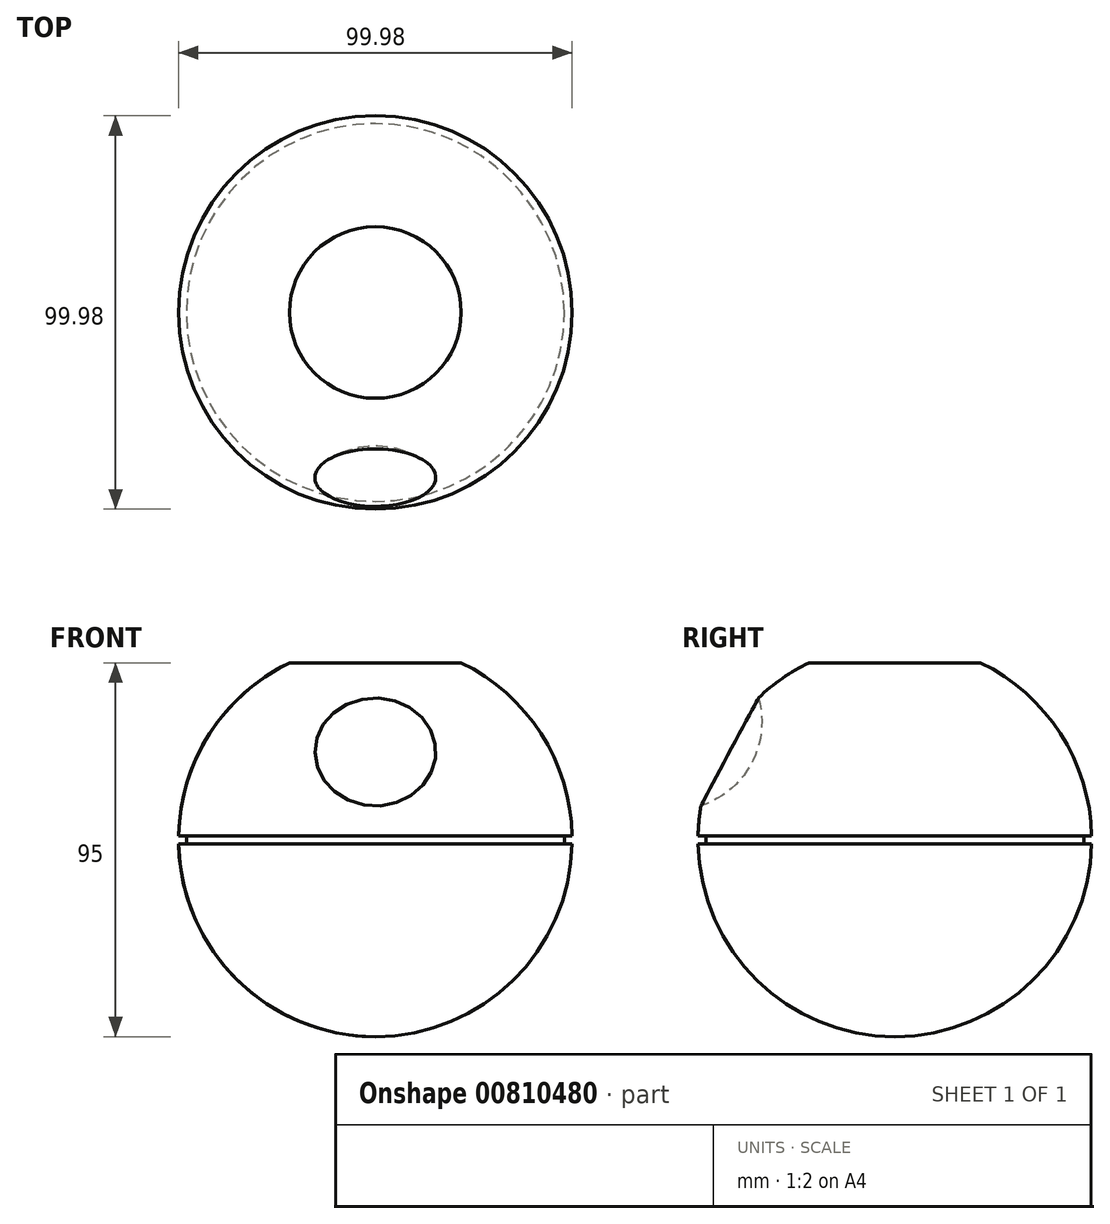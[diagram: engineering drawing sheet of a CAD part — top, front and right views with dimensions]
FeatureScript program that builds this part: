
annotation { "Feature Type Name" : "Feature", "Feature Type Description" : "" }
export const myFeature = defineFeature(function(context is Context, id is Id, definition is map)
    precondition{}
    {
        {
            var Q0;
            Q0=qCreatedBy(makeId("Front.planeOp"),FACE);
            var sketch = newSketch(context, id + "F0", { "sketchPlane" : qUnion([Q0])});
            skArc(sketch, "E0", {"start": v(0, -50) * mm, "mid": v(50, 0) * mm, "end": v(0, 50) * mm});
            skLineSegment(sketch, "E1", {"start": v(0, 50) * mm, "end": v(0, -50) * mm});
            skSolve(sketch);
        }
        {
            var Q0;
            Q0=makeQuery(id+"F0.imprint","IMPRINT",FACE,{"disambiguationData":[TD([[makeQuery(id+"F0.imprint","IMPRINT",EDGE,{"derivedFrom":sQuery(id+"F0.wireOp",EDGE,"E0")}),1.0]])]});
            var Q1;
            Q1=sQuery(id+"F0.wireOp",EDGE,"E1");
            revolve(context, id + "F1", {"entities" : qUnion([Q0]), "axis" : qUnion([Q1]), "revolveType" : RevolveType.FULL});
        }
        {
            var Q0;
            Q0=qCreatedBy(makeId("Right.planeOp"),FACE);
            var sketch = newSketch(context, id + "F2", { "sketchPlane" : qUnion([Q0])});
            skArc(sketch, "E2", {"start": v(-56.53, 7.5) * mm, "mid": v(-33.82, 29.24) * mm, "end": v(-55, 52.46) * mm});
            skLineSegment(sketch, "E3", {"start": v(-55, 52.46) * mm, "end": v(-56.53, 7.5) * mm});
            skSolve(sketch);
        }
        {
            var Q0;
            Q0=makeQuery(id+"F2.imprint","IMPRINT",FACE,{"disambiguationData":[TD([[makeQuery(id+"F2.imprint","IMPRINT",EDGE,{"derivedFrom":sQuery(id+"F2.wireOp",EDGE,"E2")}),1.0]])]});
            var Q1;
            Q1=sQuery(id+"F2.wireOp",EDGE,"E3");
            revolve(context, id + "F3", {"operationType" : NewBodyOperationType.REMOVE, "entities" : qUnion([Q0]), "axis" : qUnion([Q1]), "revolveType" : RevolveType.FULL, "oppositeDirection" : true});
        }
        {
            var Q0;
            Q0=qCreatedBy(makeId("Front.planeOp"),FACE);
            var sketch = newSketch(context, id + "F4", { "sketchPlane" : qUnion([Q0])});
            skLineSegment(sketch, "E4.bottom", {"start": v(-63.8, 61.9) * mm, "end": v(62.76, 61.9) * mm});
            skLineSegment(sketch, "E4.top", {"start": v(-63.8, 45) * mm, "end": v(62.76, 45) * mm});
            skLineSegment(sketch, "E4.left", {"start": v(-63.8, 61.9) * mm, "end": v(-63.8, 45) * mm});
            skLineSegment(sketch, "E4.right", {"start": v(62.76, 61.9) * mm, "end": v(62.76, 45) * mm});
            skSolve(sketch);
        }
        {
            var Q0;
            Q0=qSketchRegion(id+"F4",true);
            extrude(context, id + "F5", {"entities" : qUnion([Q0]), "operationType" : NewBodyOperationType.REMOVE, "oppositeDirection" : true, "depth" : 25 * mm, "hasSecondDirection" : true, "secondDirectionOppositeDirection" : false, "secondDirectionDepth" : 25 * mm});
        }
        {
            var Q0;
            Q0=qCreatedBy(makeId("Front.planeOp"),FACE);
            var sketch = newSketch(context, id + "F6", { "sketchPlane" : qUnion([Q0])});
            skLineSegment(sketch, "E5", {"start": v(0, 53.94) * mm, "end": v(0, -53.94) * mm, "construction": true});
            skLineSegment(sketch, "E6.bottom", {"start": v(-70.83, 1) * mm, "end": v(-48, 1) * mm});
            skLineSegment(sketch, "E6.top", {"start": v(-70.83, -1) * mm, "end": v(-48, -1) * mm});
            skLineSegment(sketch, "E6.left", {"start": v(-70.83, 1) * mm, "end": v(-70.83, -1) * mm});
            skLineSegment(sketch, "E6.right", {"start": v(-48, 1) * mm, "end": v(-48, -1) * mm});
            skSolve(sketch);
        }
        {
            var Q0;
            Q0=qSketchRegion(id+"F6",true);
            var Q1;
            Q1=sQuery(id+"F6.wireOp",EDGE,"E5");
            revolve(context, id + "F7", {"operationType" : NewBodyOperationType.REMOVE, "entities" : qUnion([Q0]), "axis" : qUnion([Q1]), "revolveType" : RevolveType.FULL, "oppositeDirection" : true});
        }
    });
